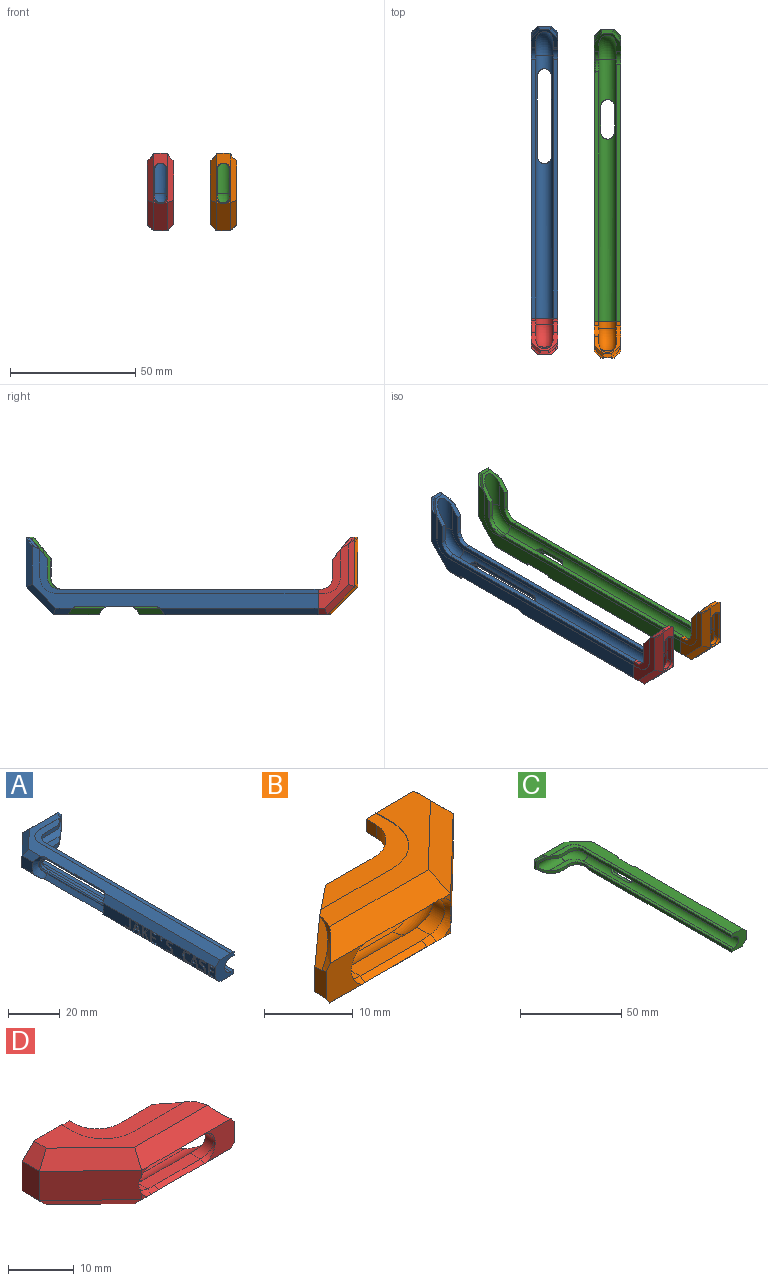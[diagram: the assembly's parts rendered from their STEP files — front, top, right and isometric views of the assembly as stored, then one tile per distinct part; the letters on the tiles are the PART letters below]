
ASSEMBLY  parts=4 mates=2
PART A: 204 faces, bbox 45.8x135.1x47.1 mm
  f0: plane 7.9x5.47mm, normal (-1,0,0), area 25.7mm2, adj f1,f2,f70,f71,f72,f73,f74,f75
  f1: plane 63.98x3.15mm, normal (-0.71,0,0.71), area 223.5mm2, adj f0,f3,f14,f15,f16,f23,f60,f79
  f2: plane 64.07x3.18mm, normal (-0.71,0,-0.71), area 223.3mm2, adj f0,f13,f14,f15,f16,f17,f18,f19
  f3: plane 114.49x25.34mm, normal (0,0,1), area 681.6mm2, adj f1,f4,f20,f22,f23,f24,f25,f26
  f4: plane 104.81x0.09mm, normal (1,0,0), area 9.4mm2, adj f3,f6,f25,f203
  f5: plane 111.18x17.53mm, normal (0,0,-1), area 227.6mm2, adj f9,f11,f31,f32,f41,f43,f48,f203
  f6: plane 111.18x17.53mm, normal (0,0,1), area 227.6mm2, adj f4,f11,f25,f26,f32,f43,f48,f203
  f7: plane 111.18x17.53mm, normal (0,0,1), area 218.9mm2, adj f9,f10,f31,f41,f42,f44,f45,f48
  f8: plane 111.18x17.53mm, normal (0,0,-1), area 218.9mm2, adj f10,f12,f42,f44,f45,f48,f50,f51
  f9: cylinder r=3.43mm len=104.81mm, axis (0,1,0), area 888.7mm2, adj f5,f7,f33,f34,f35,f36,f41,f203
  f10: plane 103.39x1.78mm, normal (1,0,0), area 183.8mm2, adj f7,f8,f42,f203
  f11: plane 103.47x1.78mm, normal (1,0,0), area 184mm2, adj f5,f6,f43,f203
  f12: plane 104.81x0.02mm, normal (1,0,0), area 2.2mm2, adj f8,f13,f51,f203
  f13: plane 114.46x25.38mm, normal (0,0,-1), area 684.8mm2, adj f2,f12,f22,f23,f30,f49,f50,f51
  f14: plane 11.2x5.47mm, normal (-1,0,0), area 33.3mm2, adj f1,f2,f60,f61,f62,f63,f64,f65
  f15: plane 38.5x6.32mm, normal (-1,0,0), area 155.2mm2, adj f1,f2,f23,f96,f97,f98,f99,f100
  f16: plane 10.36x5.51mm, normal (-1,0,0), area 38mm2, adj f1,f2,f91,f92,f93,f94,f106,f107
  f17: plane 2.88x1.67mm, normal (-1,0,0), area 3.9mm2, adj f2,f191,f197,f198
  f18: plane 2.88x1.67mm, normal (-1,0,0), area 3.9mm2, adj f2,f177,f183,f184
  f19: plane 2.57x2.17mm, normal (-1,0,0), area 3.4mm2, adj f2,f159,f170,f171
  f20: bspline ~23.11x23.11mm, area 4.9mm2, adj f3,f27,f29,f47,f53,f56
  f21: plane 11.22x10.82mm, normal (-0.69,0.72,0), area 84.7mm2, adj f28,f53,f55,f58
  f22: bspline ~16.27x7.89mm, area 45.8mm2, adj f3,f13,f24,f28,f38,f52,f54,f57
  f23: bspline ~16.27x7.89mm, area 45.8mm2, adj f1,f2,f3,f13,f15,f24,f40,f52
  f24: plane 32.32x1.6mm, normal (-0.71,0,-0.7), area 73mm2, adj f3,f22,f23,f37
  f25: cylinder r=6.37mm len=6.37mm, axis (0,0,-1), area 0.9mm2, adj f3,f4,f6,f26
  f26: plane 11.16x0.09mm, normal (0,-1,0), area 1mm2, adj f3,f6,f25,f27
  f27: bspline ~23.11x23.11mm, area 0.1mm2, adj f3,f20,f26,f48
  f28: plane 6.9x6.28mm, normal (-1,0,0), area 31.7mm2, adj f21,f22,f54,f57
  f29: plane 5.18x1.58mm, normal (1,0,0), area 7.3mm2, adj f20,f30,f46,f47,f48,f53
  f30: bspline ~23.11x23.11mm, area 4.5mm2, adj f13,f29,f46,f49,f53,f59
  f31: cylinder r=3.43mm len=15.42mm, axis (1,0,0), area 149.1mm2, adj f5,f7,f41,f48
  f32: plane 7.39x1.78mm, normal (0,-1,0), area 13.1mm2, adj f5,f6,f43,f48
  f33: cylinder r=2.8mm len=5.59mm, axis (1,0,0), area 11.4mm2, adj f9,f34,f36,f38
  f34: plane 32.32x1.37mm, normal (0,0,-1), area 44.2mm2, adj f9,f33,f35,f37
  f35: cylinder r=2.8mm len=5.59mm, axis (1,0,0), area 11.4mm2, adj f9,f34,f36,f40
  f36: plane 32.32x1.35mm, normal (0,0,1), area 43.6mm2, adj f9,f33,f35,f39
  f37: cylinder r=0.51mm len=32.32mm, axis (0,1,0), area 38.7mm2, adj f24,f34,f38,f40
  f38: bspline ~7.33x3.93mm, area 9.9mm2, adj f22,f33,f37,f39
  f39: cylinder r=0.51mm len=32.32mm, axis (0,1,0), area 38.5mm2, adj f36,f38,f40,f52
  f40: bspline ~7.33x3.94mm, area 9.9mm2, adj f23,f35,f37,f39
  f41: torus R=6.37mm, axis (0,0,-1), area 144.5mm2, adj f5,f7,f9,f31
  f42: cylinder r=4.76mm len=4.13mm, axis (0,0,-1), area 8.9mm2, adj f7,f8,f10,f45
  f43: cylinder r=4.73mm len=4.73mm, axis (0,0,1), area 13.2mm2, adj f5,f6,f11,f32
  f44: plane 7.39x1.78mm, normal (0,-1,0), area 13.1mm2, adj f7,f8,f45,f48
  f45: cylinder r=4.73mm len=2.44mm, axis (0,0,1), area 4.6mm2, adj f7,f8,f42,f44
  f46: plane 4.39x4.25mm, normal (0.56,0,-0.83), area 6.2mm2, adj f29,f30,f48
  f47: plane 4.43x4.3mm, normal (0.56,0,0.83), area 6.4mm2, adj f20,f29,f48
  f48: plane 10.41x8.65mm, normal (0.63,-0.78,0), area 36.6mm2, adj f5,f6,f7,f8,f27,f29,f31,f32
  f49: bspline ~23.11x23.11mm, area 0mm2, adj f13,f30,f48,f50
  f50: plane 11.16x0.02mm, normal (0,-1,0), area 0.2mm2, adj f8,f13,f49,f51
  f51: cylinder r=6.37mm len=6.37mm, axis (0,0,-1), area 0.2mm2, adj f8,f12,f13,f50
  f52: plane 32.32x1.63mm, normal (-0.7,0,0.72), area 73.5mm2, adj f13,f22,f23,f39
  f53: plane 19.84x5.44mm, normal (0,1,0), area 107.9mm2, adj f20,f21,f29,f30,f56,f59
  f54: plane 8.44x3.16mm, normal (-0.71,0,0.71), area 22.2mm2, adj f3,f22,f28,f55
  f55: plane 12.24x11.9mm, normal (-0.49,0.51,0.71), area 52.2mm2, adj f3,f21,f54,f56
  f56: plane 19.66x2.54mm, normal (0,0.71,0.71), area 62.4mm2, adj f3,f20,f53,f55
  f57: plane 8.52x3.17mm, normal (-0.71,0,-0.71), area 22.2mm2, adj f13,f22,f28,f58
  f58: plane 12.24x11.9mm, normal (-0.49,0.51,-0.71), area 52.2mm2, adj f13,f21,f57,f59
  f59: plane 19.76x2.54mm, normal (0,0.71,-0.71), area 62.7mm2, adj f13,f30,f53,f58
  f60: extruded ~1.3x0.76mm, area 1mm2, adj f1,f14,f61,f79,f80
  f61: extruded ~1x0.76mm, area 0.9mm2, adj f14,f60,f62,f80
  f62: extruded ~0.97x0.76mm, area 0.8mm2, adj f14,f61,f63,f80
  f63: extruded ~1.1x0.76mm, area 1mm2, adj f14,f62,f64,f80
  f64: extruded ~1.05x0.76mm, area 0.9mm2, adj f14,f63,f65,f80
  f65: extruded ~0.76x0.59mm, area 0.5mm2, adj f14,f64,f66,f80
  f66: extruded ~1.29x0.89mm, area 1.4mm2, adj f14,f65,f67,f80
  f67: extruded ~1.53x0.76mm, area 1.2mm2, adj f14,f66,f68,f80
  f68: plane 0.76x0.66mm, normal (0,-1,0), area 0.5mm2, adj f14,f67,f69,f80
  f69: extruded ~1.53x0.76mm, area 1.2mm2, adj f2,f14,f68,f70,f80
  f70: extruded ~1.45x0.76mm, area 1.1mm2, adj f0,f2,f69,f71,f80
  f71: extruded ~1.11x0.76mm, area 1mm2, adj f0,f70,f72,f80
  f72: extruded ~0.89x0.76mm, area 0.7mm2, adj f0,f71,f73,f80
  f73: extruded ~1.21x0.76mm, area 1.1mm2, adj f0,f72,f74,f80
  f74: extruded ~1x0.76mm, area 0.9mm2, adj f0,f73,f75,f80
  f75: extruded ~0.76x0.6mm, area 0.5mm2, adj f0,f74,f76,f80
  f76: extruded ~1.08x0.77mm, area 1.2mm2, adj f0,f75,f77,f80
  f77: extruded ~1.33x0.76mm, area 1mm2, adj f0,f76,f78,f80
  f78: plane 0.76x0.61mm, normal (0,0.93,0.36), area 0.5mm2, adj f0,f77,f79,f80
  f79: extruded ~1.53x0.76mm, area 1.2mm2, adj f0,f1,f60,f78,f80
  f80: plane 5.54x3.49mm, normal (-1,0,0), area 7.3mm2, adj f60,f61,f62,f63,f64,f65,f66,f67
  f81: extruded ~1.32x0.76mm, area 1mm2, adj f2,f14,f82,f94,f95
  f82: plane 0.76x0.6mm, normal (0,1,0), area 0.5mm2, adj f14,f81,f83,f95
  f83: extruded ~1.21x0.76mm, area 0.9mm2, adj f14,f82,f84,f95
  f84: extruded ~1.29x0.76mm, area 1.1mm2, adj f14,f83,f85,f95
  f85: extruded ~1.61x0.76mm, area 1.3mm2, adj f14,f84,f86,f95
  f86: extruded ~1.58x0.76mm, area 1.3mm2, adj f14,f85,f87,f95
  f87: extruded ~1.27x0.76mm, area 1.1mm2, adj f14,f86,f88,f95
  f88: extruded ~1.12x0.76mm, area 0.9mm2, adj f14,f87,f89,f95
  f89: plane 0.76x0.58mm, normal (0,0.89,0.45), area 0.5mm2, adj f14,f88,f90,f95
  f90: extruded ~1.41x0.76mm, area 1.1mm2, adj f1,f14,f89,f91,f95
  f91: extruded ~1.8x0.76mm, area 1.5mm2, adj f1,f16,f90,f92,f95
  f92: extruded ~2.02x0.76mm, area 1.7mm2, adj f16,f91,f93,f95
  f93: extruded ~2.05x0.76mm, area 1.7mm2, adj f16,f92,f94,f95
  f94: extruded ~1.74x0.76mm, area 1.5mm2, adj f2,f16,f81,f93,f95
  f95: plane 5.54x3.88mm, normal (-1,0,0), area 6.6mm2, adj f81,f82,f83,f84,f85,f86,f87,f88
  f96: extruded ~1.3x0.76mm, area 1mm2, adj f1,f15,f97,f115,f116
  f97: extruded ~1x0.76mm, area 0.9mm2, adj f15,f96,f98,f116
  f98: extruded ~0.97x0.76mm, area 0.8mm2, adj f15,f97,f99,f116
  f99: extruded ~1.1x0.76mm, area 1mm2, adj f15,f98,f100,f116
  f100: extruded ~1.05x0.76mm, area 0.9mm2, adj f15,f99,f101,f116
  f101: extruded ~0.76x0.59mm, area 0.5mm2, adj f15,f100,f102,f116
  f102: extruded ~1.29x0.89mm, area 1.4mm2, adj f15,f101,f103,f116
  f103: extruded ~1.53x0.76mm, area 1.2mm2, adj f15,f102,f104,f116
  f104: plane 0.76x0.66mm, normal (0,-1,0), area 0.5mm2, adj f15,f103,f105,f116
  f105: extruded ~1.53x0.76mm, area 1.2mm2, adj f2,f15,f104,f106,f116
  f106: extruded ~1.45x0.76mm, area 1.1mm2, adj f2,f16,f105,f107,f116
  f107: extruded ~1.11x0.76mm, area 1mm2, adj f16,f106,f108,f116
  f108: extruded ~0.89x0.76mm, area 0.7mm2, adj f16,f107,f109,f116
  f109: extruded ~1.21x0.76mm, area 1.1mm2, adj f16,f108,f110,f116
  f110: extruded ~1x0.76mm, area 0.9mm2, adj f16,f109,f111,f116
  f111: extruded ~0.76x0.6mm, area 0.5mm2, adj f16,f110,f112,f116
  f112: extruded ~1.08x0.77mm, area 1.2mm2, adj f16,f111,f113,f116
  f113: extruded ~1.33x0.76mm, area 1mm2, adj f16,f112,f114,f116
  f114: plane 0.76x0.61mm, normal (0,0.93,0.36), area 0.5mm2, adj f16,f113,f115,f116
  f115: extruded ~1.53x0.76mm, area 1.2mm2, adj f1,f16,f96,f114,f116
  f116: plane 5.54x3.49mm, normal (-1,0,0), area 7.3mm2, adj f96,f97,f98,f99,f100,f101,f102,f103
  f117: extruded ~1.39x0.76mm, area 1.1mm2, adj f2,f15,f118,f126,f127
  f118: extruded ~1.27x0.76mm, area 1.1mm2, adj f15,f117,f119,f127
  f119: plane 3.73x0.76mm, normal (0,1,0), area 2.8mm2, adj f15,f118,f120,f127
  f120: plane 0.76x0.69mm, normal (0,0,-1), area 0.5mm2, adj f15,f119,f121,f127
  f121: plane 3.74x0.76mm, normal (0,-1,0), area 2.8mm2, adj f15,f120,f122,f127
  f122: extruded ~0.83x0.76mm, area 0.7mm2, adj f15,f121,f123,f127
  f123: extruded ~0.94x0.76mm, area 0.8mm2, adj f15,f122,f124,f127
  f124: extruded ~1.14x0.76mm, area 0.9mm2, adj f15,f123,f125,f127
  f125: plane 0.76x0.61mm, normal (0,-1,0), area 0.5mm2, adj f15,f124,f126,f127
  f126: extruded ~1.2x0.76mm, area 0.9mm2, adj f2,f15,f117,f125,f127
  f127: plane 5.47x3.1mm, normal (-1,0,0), area 4.9mm2, adj f117,f118,f119,f120,f121,f122,f123,f124
  f128: plane 5.39x0.76mm, normal (0,-1,0), area 4.1mm2, adj f15,f129,f139,f140
  f129: plane 3.1x0.76mm, normal (0,0,1), area 2.4mm2, adj f2,f128,f130,f140
  f130: plane 0.76x0.61mm, normal (0,1,0), area 0.5mm2, adj f15,f129,f131,f140
  f131: plane 2.42x0.76mm, normal (0,0,-1), area 1.8mm2, adj f15,f130,f132,f140
  f132: plane 1.92x0.76mm, normal (0,1,0), area 1.5mm2, adj f15,f131,f133,f140
  f133: plane 2.28x0.76mm, normal (0,0,1), area 1.7mm2, adj f15,f132,f134,f140
  f134: plane 0.76x0.6mm, normal (0,1,0), area 0.5mm2, adj f15,f133,f135,f140
  f135: plane 2.28x0.76mm, normal (0,0,-1), area 1.7mm2, adj f15,f134,f136,f140
  f136: plane 1.67x0.76mm, normal (0,1,0), area 1.3mm2, adj f15,f135,f137,f140
  f137: plane 2.42x0.76mm, normal (0,0,1), area 1.8mm2, adj f15,f136,f138,f140
  f138: plane 0.76x0.61mm, normal (0,1,0), area 0.5mm2, adj f15,f137,f139,f140
  f139: plane 3.1x0.76mm, normal (0,0,-1), area 2.4mm2, adj f15,f128,f138,f140
  f140: plane 5.39x3.1mm, normal (-1,0,0), area 8mm2, adj f128,f129,f130,f131,f132,f133,f134,f135
  f141: plane 1.95x0.76mm, normal (0,1,0.08), area 1.5mm2, adj f15,f142,f144,f145
  f142: plane 0.87x0.76mm, normal (0,0,-1), area 0.7mm2, adj f15,f141,f143,f145
  f143: plane 1.95x0.76mm, normal (0,-1,0.08), area 1.5mm2, adj f15,f142,f144,f145
  f144: plane 0.76x0.57mm, normal (0,0,1), area 0.4mm2, adj f15,f141,f143,f145
  f145: plane 1.95x0.87mm, normal (-1,0,0), area 1.4mm2, adj f141,f142,f143,f144
  f146: plane 5.39x0.76mm, normal (0,-1,0), area 4.1mm2, adj f0,f147,f157,f158
  f147: plane 3.1x0.76mm, normal (0,0,1), area 2.4mm2, adj f2,f146,f148,f158
  f148: plane 0.76x0.61mm, normal (0,1,0), area 0.5mm2, adj f0,f147,f149,f158
  f149: plane 2.42x0.76mm, normal (0,0,-1), area 1.8mm2, adj f0,f148,f150,f158
  f150: plane 1.92x0.76mm, normal (0,1,0), area 1.5mm2, adj f0,f149,f151,f158
  f151: plane 2.28x0.76mm, normal (0,0,1), area 1.7mm2, adj f0,f150,f152,f158
  f152: plane 0.76x0.6mm, normal (0,1,0), area 0.5mm2, adj f0,f151,f153,f158
  f153: plane 2.28x0.76mm, normal (0,0,-1), area 1.7mm2, adj f0,f152,f154,f158
  f154: plane 1.67x0.76mm, normal (0,1,0), area 1.3mm2, adj f0,f153,f155,f158
  f155: plane 2.42x0.76mm, normal (0,0,1), area 1.8mm2, adj f0,f154,f156,f158
  f156: plane 0.76x0.61mm, normal (0,1,0), area 0.5mm2, adj f0,f155,f157,f158
  f157: plane 3.1x0.76mm, normal (0,0,-1), area 2.4mm2, adj f0,f146,f156,f158
  f158: plane 5.39x3.1mm, normal (-1,0,0), area 8mm2, adj f146,f147,f148,f149,f150,f151,f152,f153
  f159: plane 2.57x1.66mm, normal (0,-0.84,0.54), area 2.3mm2, adj f19,f160,f171,f172
  f160: plane 0.78x0.76mm, normal (0,0,1), area 0.6mm2, adj f2,f159,f161,f172
  f161: plane 3.04x1.99mm, normal (0,0.84,-0.55), area 2.8mm2, adj f15,f160,f162,f172
  f162: plane 2.35x1.92mm, normal (0,0.77,0.63), area 2.3mm2, adj f15,f161,f163,f172
  f163: plane 0.77x0.76mm, normal (0,0,-1), area 0.6mm2, adj f15,f162,f164,f172
  f164: plane 2.08x1.67mm, normal (0,-0.78,-0.63), area 2mm2, adj f15,f163,f165,f172
  f165: plane 0.76x0.62mm, normal (0,-0.81,-0.58), area 0.6mm2, adj f15,f164,f166,f172
  f166: plane 2.7x0.76mm, normal (0,1,0), area 2.1mm2, adj f15,f165,f167,f172
  f167: plane 0.76x0.69mm, normal (0,0,-1), area 0.5mm2, adj f15,f166,f168,f172
  f168: plane 5.39x0.76mm, normal (0,-1,0), area 4.1mm2, adj f15,f167,f169,f172
  f169: plane 0.76x0.69mm, normal (0,0,1), area 0.5mm2, adj f2,f168,f170,f172
  f170: plane 2.15x0.76mm, normal (0,1,0), area 1.6mm2, adj f19,f169,f171,f172
  f171: plane 0.76x0.52mm, normal (0,0.63,0.78), area 0.5mm2, adj f19,f159,f170,f172
  f172: plane 5.39x3.64mm, normal (-1,0,0), area 8mm2, adj f159,f160,f161,f162,f163,f164,f165,f166
  f173: plane 1.56x0.76mm, normal (0,-0.95,0.3), area 1.2mm2, adj f174,f185,f186,f201
  f174: plane 1.42x0.76mm, normal (0,0,-1), area 1.1mm2, adj f173,f175,f186,f201
  f175: plane 1.72x0.76mm, normal (0,0.96,0.29), area 1.4mm2, adj f174,f176,f186,f201
  f176: extruded ~0.76x0.68mm, area 0.5mm2, adj f175,f185,f186,f201
  f177: plane 1.67x0.76mm, normal (0,-0.95,0.3), area 1.3mm2, adj f18,f178,f184,f186
  f178: plane 0.76x0.71mm, normal (0,0,1), area 0.5mm2, adj f2,f177,f179,f186
  f179: plane 5.41x1.79mm, normal (0,0.95,-0.31), area 4.3mm2, adj f15,f178,f180,f186
  f180: plane 0.76x0.72mm, normal (0,0,-1), area 0.5mm2, adj f15,f179,f181,f186
  f181: plane 5.41x1.78mm, normal (0,-0.95,-0.31), area 4.3mm2, adj f15,f180,f182,f186
  f182: plane 0.76x0.7mm, normal (0,0,1), area 0.5mm2, adj f2,f181,f183,f186
  f183: plane 1.67x0.76mm, normal (0,0.95,0.31), area 1.3mm2, adj f18,f182,f184,f186
  f184: plane 1.81x0.76mm, normal (0,0,1), area 1.4mm2, adj f18,f177,f183,f186
  f185: extruded ~0.83x0.76mm, area 0.7mm2, adj f173,f176,f186,f201
  f186: plane 5.41x4.29mm, normal (-1,0,0), area 8mm2, adj f173,f174,f175,f176,f177,f178,f179,f180
  f187: plane 1.56x0.76mm, normal (0,-0.95,0.3), area 1.2mm2, adj f188,f199,f200,f202
  f188: plane 1.42x0.76mm, normal (0,0,-1), area 1.1mm2, adj f187,f189,f200,f202
  f189: plane 1.72x0.76mm, normal (0,0.96,0.29), area 1.4mm2, adj f188,f190,f200,f202
  f190: extruded ~0.76x0.68mm, area 0.5mm2, adj f189,f199,f200,f202
  f191: plane 1.67x0.76mm, normal (0,-0.95,0.3), area 1.3mm2, adj f17,f192,f198,f200
  f192: plane 0.76x0.71mm, normal (0,0,1), area 0.5mm2, adj f2,f191,f193,f200
  f193: plane 5.41x1.79mm, normal (0,0.95,-0.31), area 4.3mm2, adj f14,f192,f194,f200
  f194: plane 0.76x0.72mm, normal (0,0,-1), area 0.5mm2, adj f14,f193,f195,f200
  f195: plane 5.41x1.78mm, normal (0,-0.95,-0.31), area 4.3mm2, adj f14,f194,f196,f200
  f196: plane 0.76x0.7mm, normal (0,0,1), area 0.5mm2, adj f2,f195,f197,f200
  f197: plane 1.67x0.76mm, normal (0,0.95,0.31), area 1.3mm2, adj f17,f196,f198,f200
  f198: plane 1.81x0.76mm, normal (0,0,1), area 1.4mm2, adj f17,f191,f197,f200
  f199: extruded ~0.83x0.76mm, area 0.7mm2, adj f187,f190,f200,f202
  f200: plane 5.41x4.29mm, normal (-1,0,0), area 8mm2, adj f187,f188,f189,f190,f191,f192,f193,f194
  f201: plane 2.4x1.42mm, normal (-1,0,0), area 1.6mm2, adj f173,f174,f175,f176,f185
  f202: plane 2.4x1.42mm, normal (-1,0,0), area 1.6mm2, adj f187,f188,f189,f190,f199
  f203: plane 10.52x10.26mm, normal (0,-1,0), area 71.2mm2, adj f0,f1,f2,f3,f4,f5,f6,f7
PART B: 52 faces, bbox 38.9x34.7x46.3 mm
  f0: plane 25.42x12.03mm, normal (0,0,1), area 92.7mm2, adj f37,f38,f39,f40,f42,f46,f47,f50
  f1: plane 6.1x5.47mm, normal (0,-1,0), area 24.2mm2, adj f6,f11,f41,f42,f49,f50
  f2: plane 1.46x1.21mm, normal (0,-1,0), area 0.6mm2, adj f4,f35,f50
  f3: plane 25.44x12mm, normal (0,0,-1), area 92.8mm2, adj f6,f7,f8,f9,f10,f44,f45,f49
  f4: plane 11.22x10.82mm, normal (0.69,-0.72,0), area 83.7mm2, adj f2,f35,f43,f45,f47,f48
  f5: plane 9.77x0.85mm, normal (0,-0.45,0.89), area 9.3mm2, adj f22,f36,f41,f49
  f6: bspline ~23.11x23.11mm, area 4.6mm2, adj f1,f3,f7,f11,f31,f49
  f7: bspline ~23.11x23.11mm, area 0mm2, adj f3,f6,f8,f12
  f8: plane 11.4x0.02mm, normal (0,1,0), area 0.2mm2, adj f3,f7,f9,f14
  f9: cylinder r=6.37mm len=6.37mm, axis (0,0,-1), area 0.2mm2, adj f3,f8,f10,f14
  f10: plane 2.59x0.02mm, normal (-1,0,0), area 0.1mm2, adj f3,f9,f14,f51
  f11: plane 3.95x1.79mm, normal (-1,0,0), area 6.4mm2, adj f1,f6,f12,f31,f32,f42
  f12: plane 10.41x8.6mm, normal (-0.63,0.78,0), area 33.8mm2, adj f7,f11,f13,f14,f15,f16,f18,f25
  f13: plane 17.77x8.96mm, normal (0,0,1), area 53.7mm2, adj f12,f17,f18,f19,f20,f25,f29,f30
  f14: plane 17.77x8.96mm, normal (0,0,-1), area 53.7mm2, adj f8,f9,f10,f12,f17,f25,f29,f30
  f15: plane 17.77x8.96mm, normal (0,0,-1), area 54.1mm2, adj f12,f18,f19,f20,f26,f27,f28,f51
  f16: plane 17.77x8.96mm, normal (0,0,1), area 54.1mm2, adj f12,f26,f27,f28,f37,f38,f39,f51
  f17: cylinder r=4.73mm len=1.78mm, axis (0,0,-1), area 1.5mm2, adj f13,f14,f25,f29
  f18: cylinder r=3.43mm len=15.68mm, axis (-1,0,0), area 92.9mm2, adj f12,f13,f15,f19,f21,f22,f24
  f19: torus R=6.37mm, axis (0,0,-1), area 127.5mm2, adj f13,f15,f18,f20,f22,f23,f24
  f20: cylinder r=3.43mm len=6.85mm, axis (0,-1,0), area 27.9mm2, adj f13,f15,f19,f51
  f21: cylinder r=2.32mm len=4.65mm, axis (0,1,0), area 15.6mm2, adj f18,f22,f24,f41
  f22: plane 11.25x2.27mm, normal (0,0,1), area 24.1mm2, adj f5,f18,f19,f21,f23,f36
  f23: cylinder r=2.32mm len=4.65mm, axis (0,1,0), area 15.8mm2, adj f19,f22,f24,f35
  f24: plane 11.25x2.26mm, normal (0,0,-1), area 24.1mm2, adj f18,f19,f21,f23,f33,f34
  f25: plane 7.58x1.78mm, normal (0,1,0), area 13.5mm2, adj f12,f13,f14,f17
  f26: plane 1.78x1.69mm, normal (-1,0,0), area 3mm2, adj f15,f16,f27,f51
  f27: cylinder r=4.79mm len=5.35mm, axis (0,0,1), area 13.4mm2, adj f15,f16,f26,f28
  f28: plane 7.01x1.78mm, normal (0,1,0), area 12.5mm2, adj f12,f15,f16,f27
  f29: cylinder r=4.79mm len=4.14mm, axis (0,0,1), area 11mm2, adj f13,f14,f17,f30
  f30: plane 1.78x1.69mm, normal (-1,0,0), area 3mm2, adj f13,f14,f29,f51
  f31: plane 4.18x3.82mm, normal (-0.67,0,-0.75), area 7mm2, adj f6,f11,f12
  f32: plane 4.2x3.84mm, normal (-0.67,0,0.75), area 7.1mm2, adj f11,f12,f42
  f33: plane 9.77x0.9mm, normal (0,-0.45,-0.9), area 9.9mm2, adj f24,f34,f41,f50
  f34: cone r=11.03mm half-angle=63.5deg, axis (0,0,1), area 1.6mm2, adj f24,f33,f35,f50
  f35: bspline ~10.32x6.08mm, area 8.3mm2, adj f2,f4,f23,f34,f36,f48,f49,f50
  f36: cone r=11.02mm half-angle=63.4deg, axis (0,0,-1), area 1.5mm2, adj f5,f22,f35,f49
  f37: plane 2.59x0.09mm, normal (-1,0,0), area 0.2mm2, adj f0,f16,f38,f51
  f38: cylinder r=6.37mm len=6.37mm, axis (0,0,-1), area 0.9mm2, adj f0,f16,f37,f39
  f39: plane 11.4x0.09mm, normal (0,1,0), area 1mm2, adj f0,f16,f38,f40
  f40: bspline ~23.11x23.11mm, area 0.1mm2, adj f0,f12,f39,f42
  f41: bspline ~10.32x6.9mm, area 5.2mm2, adj f1,f5,f21,f33,f49,f50
  f42: bspline ~23.11x23.11mm, area 5mm2, adj f0,f1,f11,f32,f40,f50
  f43: plane 5.44x3.72mm, normal (1,0,0), area 20.2mm2, adj f4,f44,f46,f51
  f44: plane 3.72x2.54mm, normal (0.71,0,-0.71), area 11.4mm2, adj f3,f43,f45,f51
  f45: plane 12.24x11.9mm, normal (0.49,-0.51,-0.71), area 52.2mm2, adj f3,f4,f44,f49
  f46: plane 3.72x2.54mm, normal (0.71,0,0.71), area 11.4mm2, adj f0,f43,f47,f51
  f47: plane 12.24x11.9mm, normal (0.49,-0.51,0.71), area 52.2mm2, adj f0,f4,f46,f50
  f48: plane 1.2x1.1mm, normal (0,-1,0), area 0.5mm2, adj f4,f35,f49
  f49: plane 19.32x2.59mm, normal (0,-0.71,-0.71), area 61.2mm2, adj f1,f3,f5,f6,f35,f36,f41,f45
  f50: plane 19.24x2.58mm, normal (0,-0.71,0.71), area 61.9mm2, adj f0,f1,f2,f33,f34,f35,f41,f42
  f51: plane 10.52x10.1mm, normal (0,1,0), area 70.7mm2, adj f0,f3,f10,f13,f14,f15,f16,f20
PART C: 57 faces, bbox 45.8x135.1x47.1 mm
  f0: plane 17.81x6.28mm, normal (1,0,0), area 91.1mm2, adj f1,f14,f17,f18
  f1: plane 11.22x10.82mm, normal (0.69,0.72,0), area 84.7mm2, adj f0,f2,f13,f19
  f2: plane 19.84x5.44mm, normal (0,1,0), area 107.9mm2, adj f1,f4,f11,f12,f20,f21
  f3: plane 4.39x4.25mm, normal (-0.56,0,-0.83), area 6.2mm2, adj f4,f21,f30
  f4: plane 5.18x1.58mm, normal (-1,0,0), area 7.3mm2, adj f2,f3,f5,f11,f21,f30
  f5: plane 4.43x4.3mm, normal (-0.56,0,0.83), area 6.4mm2, adj f4,f11,f30
  f6: cylinder r=0.51mm len=10.2mm, axis (0,-1,0), area 12.1mm2, adj f8,f9,f16,f33
  f7: cylinder r=0.51mm len=10.2mm, axis (0,-1,0), area 12.2mm2, adj f8,f9,f15,f35
  f8: bspline ~7.32x3.93mm, area 9.9mm2, adj f6,f7,f17,f36
  f9: bspline ~7.32x3.47mm, area 9.9mm2, adj f6,f7,f34,f41
  f10: bspline ~23.11x23.11mm, area 0.1mm2, adj f11,f30,f31,f55
  f11: bspline ~23.11x23.11mm, area 4.9mm2, adj f2,f4,f5,f10,f12,f55
  f12: plane 19.66x2.54mm, normal (0,0.71,0.71), area 62.4mm2, adj f2,f11,f13,f55
  f13: plane 12.24x11.9mm, normal (0.49,0.51,0.71), area 52.2mm2, adj f1,f12,f14,f55
  f14: plane 19.35x3.15mm, normal (0.71,0,0.71), area 61.4mm2, adj f0,f13,f17,f55
  f15: plane 10.2x1.61mm, normal (0.71,0,-0.71), area 23.1mm2, adj f7,f17,f41,f55
  f16: plane 10.2x1.63mm, normal (0.7,0,0.72), area 23.3mm2, adj f6,f17,f41,f54
  f17: bspline ~16.25x7.89mm, area 45.7mm2, adj f0,f8,f14,f15,f16,f18,f54,f55
  f18: plane 19.45x3.18mm, normal (0.71,0,-0.71), area 61.4mm2, adj f0,f17,f19,f54
  f19: plane 12.24x11.9mm, normal (0.49,0.51,-0.71), area 52.2mm2, adj f1,f18,f20,f54
  f20: plane 19.76x2.54mm, normal (0,0.71,-0.71), area 62.7mm2, adj f2,f19,f21,f54
  f21: bspline ~23.11x23.11mm, area 4.5mm2, adj f2,f3,f4,f20,f22,f54
  f22: bspline ~23.11x23.11mm, area 0mm2, adj f21,f26,f30,f54
  f23: cylinder r=4.77mm len=5.11mm, axis (0,0,1), area 11.1mm2, adj f24,f27,f38,f39,f49
  f24: plane 6.95x1.69mm, normal (0,-1,0), area 11.8mm2, adj f23,f27,f30,f49
  f25: cylinder r=6.37mm len=6.37mm, axis (0,0,-1), area 0.2mm2, adj f26,f43,f50,f54
  f26: plane 11.16x0.02mm, normal (0,-1,0), area 0.2mm2, adj f22,f25,f43,f54
  f27: cylinder r=0.51mm len=7.39mm, axis (-1,0,0), area 2.1mm2, adj f23,f24,f30,f38,f43
  f28: cylinder r=3.43mm len=15.42mm, axis (1,0,0), area 149.1mm2, adj f30,f32,f48,f49
  f29: plane 6.95x1.78mm, normal (0,-1,0), area 12.4mm2, adj f30,f37,f46,f48
  f30: plane 10.42x8.67mm, normal (-0.63,-0.78,0), area 36.6mm2, adj f3,f4,f5,f10,f22,f24,f27,f28
  f31: plane 11.16x0.09mm, normal (0,-1,0), area 1mm2, adj f10,f40,f46,f55
  f32: torus R=6.37mm, axis (0,0,-1), area 144.5mm2, adj f28,f47,f48,f49
  f33: plane 10.2x1.35mm, normal (0,0,1), area 13.7mm2, adj f6,f34,f36,f47
  f34: cylinder r=2.79mm len=5.59mm, axis (-1,0,0), area 11.4mm2, adj f9,f33,f35,f47
  f35: plane 10.2x1.37mm, normal (0,0,-1), area 13.9mm2, adj f7,f34,f36,f47
  f36: cylinder r=2.79mm len=5.59mm, axis (-1,0,0), area 11.4mm2, adj f8,f33,f35,f47
  f37: cylinder r=4.77mm len=5.35mm, axis (0,0,1), area 15.4mm2, adj f29,f45,f46,f48
  f38: torus R=6.22mm, axis (0,0,-1), area 6.4mm2, adj f23,f27,f39,f42,f43
  f39: cylinder r=5.71mm len=5.03mm, axis (0,0,1), area 6.6mm2, adj f23,f38,f42,f49
  f40: cylinder r=6.37mm len=6.37mm, axis (0,0,-1), area 0.9mm2, adj f31,f44,f46,f55
  f41: bspline ~16.25x7.88mm, area 45.7mm2, adj f9,f15,f16,f51,f52,f53,f54,f55
  f42: plane 100.16x1.98mm, normal (-1,0,0), area 177.6mm2, adj f38,f39,f43,f49,f56
  f43: plane 111.18x17.53mm, normal (0,0,-1), area 202.3mm2, adj f25,f26,f27,f30,f38,f42,f50,f56
  f44: plane 104.81x0.09mm, normal (-1,0,0), area 9.4mm2, adj f40,f46,f55,f56
  f45: plane 102.88x1.78mm, normal (-1,0,0), area 182.9mm2, adj f37,f46,f48,f56
  f46: plane 111.18x17.53mm, normal (0,0,1), area 210.4mm2, adj f29,f30,f31,f37,f40,f44,f45,f56
  f47: cylinder r=3.43mm len=104.81mm, axis (0,-1,0), area 1033.7mm2, adj f32,f33,f34,f35,f36,f48,f49,f56
  f48: plane 111.18x17.53mm, normal (0,0,-1), area 210.4mm2, adj f28,f29,f30,f32,f37,f45,f47,f56
  f49: plane 111.18x17.53mm, normal (0,0,1), area 208.9mm2, adj f23,f24,f28,f30,f32,f39,f42,f47
  f50: plane 104.81x0.02mm, normal (-1,0,0), area 2.2mm2, adj f25,f43,f54,f56
  f51: plane 75.21x3.16mm, normal (0.71,0,0.71), area 263.9mm2, adj f41,f53,f55,f56
  f52: plane 75.29x3.17mm, normal (0.71,0,-0.71), area 264mm2, adj f41,f53,f54,f56
  f53: plane 73.66x6.28mm, normal (1,0,0), area 394.7mm2, adj f41,f51,f52,f56
  f54: plane 114.45x25.37mm, normal (0,0,-1), area 699.9mm2, adj f16,f17,f18,f19,f20,f21,f22,f25
  f55: plane 114.48x25.34mm, normal (0,0,1), area 698.7mm2, adj f10,f11,f12,f13,f14,f15,f17,f31
  f56: plane 10.52x10.11mm, normal (0,-1,0), area 70.7mm2, adj f42,f43,f44,f45,f46,f47,f48,f49
PART D: 51 faces, bbox 38.9x34.7x46.3 mm
  f0: plane 9.77x0.9mm, normal (0,-0.45,-0.9), area 9.9mm2, adj f1,f6,f12,f18
  f1: cone r=11.03mm half-angle=63.5deg, axis (0,0,1), area 1.6mm2, adj f0,f6,f9,f18
  f2: plane 1.46x1.21mm, normal (0,-1,0), area 0.6mm2, adj f9,f18,f19
  f3: cylinder r=2.32mm len=4.65mm, axis (0,1,0), area 12.2mm2, adj f6,f7,f12,f24
  f4: plane 3.93x3.79mm, normal (0.67,0,0.75), area 5.8mm2, adj f13,f17,f25
  f5: cylinder r=2.32mm len=4.65mm, axis (0,1,0), area 15.8mm2, adj f6,f7,f9,f27
  f6: plane 11.25x2.26mm, normal (0,0,-1), area 24.1mm2, adj f0,f1,f3,f5,f24,f27
  f7: plane 11.25x2.27mm, normal (0,0,1), area 24.1mm2, adj f3,f5,f10,f11,f24,f27
  f8: plane 1.2x1.1mm, normal (0,-1,0), area 0.5mm2, adj f9,f19,f31
  f9: bspline ~10.32x6.08mm, area 8.3mm2, adj f1,f2,f5,f8,f10,f18,f19,f31
  f10: cone r=11.02mm half-angle=63.4deg, axis (0,0,-1), area 1.5mm2, adj f7,f9,f11,f31
  f11: plane 9.77x0.85mm, normal (0,-0.45,0.89), area 9.3mm2, adj f7,f10,f12,f31
  f12: bspline ~10.32x6.9mm, area 5.2mm2, adj f0,f3,f11,f15,f18,f31
  f13: plane 3.95x1.52mm, normal (1,0,0), area 5.5mm2, adj f4,f14,f15,f17,f25,f32
  f14: plane 3.9x3.77mm, normal (0.67,0,-0.75), area 5.7mm2, adj f13,f25,f32
  f15: plane 6.1x5.47mm, normal (0,-1,0), area 24.2mm2, adj f12,f13,f17,f18,f31,f32
  f16: bspline ~23.11x23.11mm, area 0.2mm2, adj f17,f22,f25,f49
  f17: bspline ~23.11x23.11mm, area 5mm2, adj f4,f13,f15,f16,f18,f49
  f18: plane 19.24x2.58mm, normal (0,-0.71,0.71), area 61.9mm2, adj f0,f1,f2,f9,f12,f15,f17,f20
  f19: plane 11.22x10.82mm, normal (-0.69,-0.72,0), area 83.7mm2, adj f2,f8,f9,f20,f30,f48
  f20: plane 12.24x11.9mm, normal (-0.49,-0.51,0.71), area 52.2mm2, adj f18,f19,f36,f49
  f21: plane 7.21x1.78mm, normal (0,1,0), area 12.8mm2, adj f25,f29,f44,f45
  f22: plane 11.12x0.09mm, normal (0,1,0), area 1mm2, adj f16,f23,f44,f49
  f23: cylinder r=6.37mm len=6.37mm, axis (0,0,-1), area 0.9mm2, adj f22,f44,f46,f49
  f24: cylinder r=3.43mm len=15.35mm, axis (-1,0,0), area 89.6mm2, adj f3,f6,f7,f25,f27,f42,f45
  f25: plane 10.41x8.84mm, normal (0.63,0.78,0), area 37.7mm2, adj f4,f13,f14,f16,f21,f24,f26,f33
  f26: plane 7.35x1.78mm, normal (0,1,0), area 13.1mm2, adj f25,f28,f41,f42
  f27: torus R=6.37mm, axis (0,0,-1), area 127.5mm2, adj f5,f6,f7,f24,f37,f42,f45
  f28: cylinder r=4.73mm len=4.73mm, axis (0,0,-1), area 13.2mm2, adj f26,f40,f41,f42
  f29: cylinder r=4.76mm len=4.76mm, axis (0,0,1), area 13.3mm2, adj f21,f43,f44,f45
  f30: plane 12.24x11.9mm, normal (-0.49,-0.51,-0.71), area 52.2mm2, adj f19,f31,f38,f47
  f31: plane 19.32x2.59mm, normal (0,-0.71,-0.71), area 61.2mm2, adj f8,f9,f10,f11,f12,f15,f30,f32
  f32: bspline ~23.11x23.11mm, area 4.6mm2, adj f13,f14,f15,f31,f33,f38
  f33: bspline ~23.11x23.11mm, area 0.1mm2, adj f25,f32,f34,f38
  f34: plane 11.12x0.02mm, normal (0,1,0), area 0.2mm2, adj f33,f35,f38,f41
  f35: cylinder r=6.37mm len=6.37mm, axis (0,0,-1), area 0.2mm2, adj f34,f38,f39,f41
  f36: plane 3.72x2.54mm, normal (-0.71,0,0.71), area 11.4mm2, adj f20,f48,f49,f50
  f37: cylinder r=3.43mm len=6.85mm, axis (0,1,0), area 27.9mm2, adj f27,f42,f45,f50
  f38: plane 25.43x12mm, normal (0,0,-1), area 92.5mm2, adj f30,f31,f32,f33,f34,f35,f39,f47
  f39: plane 2.59x0.02mm, normal (1,0,0), area 0.1mm2, adj f35,f38,f41,f50
  f40: plane 1.78x1.18mm, normal (1,0,0), area 2.1mm2, adj f28,f41,f42,f50
  f41: plane 17.49x8.96mm, normal (0,0,-1), area 53.5mm2, adj f25,f26,f28,f34,f35,f39,f40,f50
  f42: plane 17.49x8.96mm, normal (0,0,1), area 53.5mm2, adj f24,f25,f26,f27,f28,f37,f40,f50
  f43: plane 1.78x1.1mm, normal (1,0,0), area 2mm2, adj f29,f44,f45,f50
  f44: plane 17.49x8.96mm, normal (0,0,1), area 54.4mm2, adj f21,f22,f23,f25,f29,f43,f46,f50
  f45: plane 17.49x8.96mm, normal (0,0,-1), area 54.4mm2, adj f21,f24,f25,f27,f29,f37,f43,f50
  f46: plane 2.59x0.09mm, normal (1,0,0), area 0.2mm2, adj f23,f44,f49,f50
  f47: plane 3.72x2.54mm, normal (-0.71,0,-0.71), area 11.4mm2, adj f30,f38,f48,f50
  f48: plane 5.44x3.72mm, normal (-1,0,0), area 20.2mm2, adj f19,f36,f47,f50
  f49: plane 25.45x12.05mm, normal (0,0,1), area 92.5mm2, adj f16,f17,f18,f20,f22,f23,f36,f46
  f50: plane 10.52x10.26mm, normal (0,1,0), area 71.2mm2, adj f36,f37,f38,f39,f40,f41,f42,f43
PLACE A rot(axis=(0,-1,0),90deg) t=(4.97,9.26,38.7)mm
PLACE B rot(axis=(0,1,0),90deg) t=(20.57,21.79,38.7)mm
PLACE C rot(axis=(0,1,0),90deg) t=(20.57,7.82,38.7)mm
PLACE D rot(axis=(0,-1,0),90deg) t=(4.97,23.23,38.7)mm
MATE fastened D.f50 <-> A.f203  axis (0,1,0) through (0.13,-34.87,4.29)mm
MATE fastened C.f56 <-> B.f51  axis (0,-1,0) through (25.41,-36.3,4.25)mm
